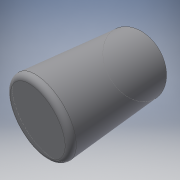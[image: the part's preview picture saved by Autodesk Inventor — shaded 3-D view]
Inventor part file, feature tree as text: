
AUTODESK INVENTOR PART (.ipt)
format: ipt  version: 2019 (Build 230136000, 136)  size: 109,056 bytes
history: native  units: in
note: dims shown in document units (in); Inventor stores cm internally (conversion verified against a paired STEP export)
features: extrude x1, fillet x1, sketch x1
ambient origin geometry x8: Origin, YZ Plane, XZ Plane, XY Plane, X Axis, Y Axis, Z Axis, Center Point
bodies: Solid1 (feature_tree)
feature tree (3):
  extrude  "Extrusion1"  Depth=2.62in TaperAngle=0.0deg
  fillet  "Fillet1"  Radius=0.125in
  sketch  "Sketch1"  dims[d0=1.76in d1=2.62in d2=0.0in d3=0.125in]
